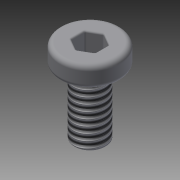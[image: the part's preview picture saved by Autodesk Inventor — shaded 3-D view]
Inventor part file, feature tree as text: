
AUTODESK INVENTOR PART (.ipt)
format: ipt  version: 2013 (Build 170138000, 138)  size: 163,328 bytes
history: native  units: mm
features: extrude x3, sketch x3, fillet x2, other x1, thread x1
ambient origin geometry x1: Origin
feature tree (10):
  other  "ソリッド1"
  extrude  "押し出し1"  Depth=3.8mm
  extrude  "押し出し2"  Depth=1.3mm TaperAngle=0.0deg
  extrude  "押し出し3"  Depth=2.0mm
  fillet  "フィレット1"  Radius=4.0mm
  fillet  "フィレット2"  Radius=0.75mm
  thread  "ねじ3"
  sketch  "スケッチ1"
  sketch  "スケッチ2"
  sketch  "スケッチ3"
